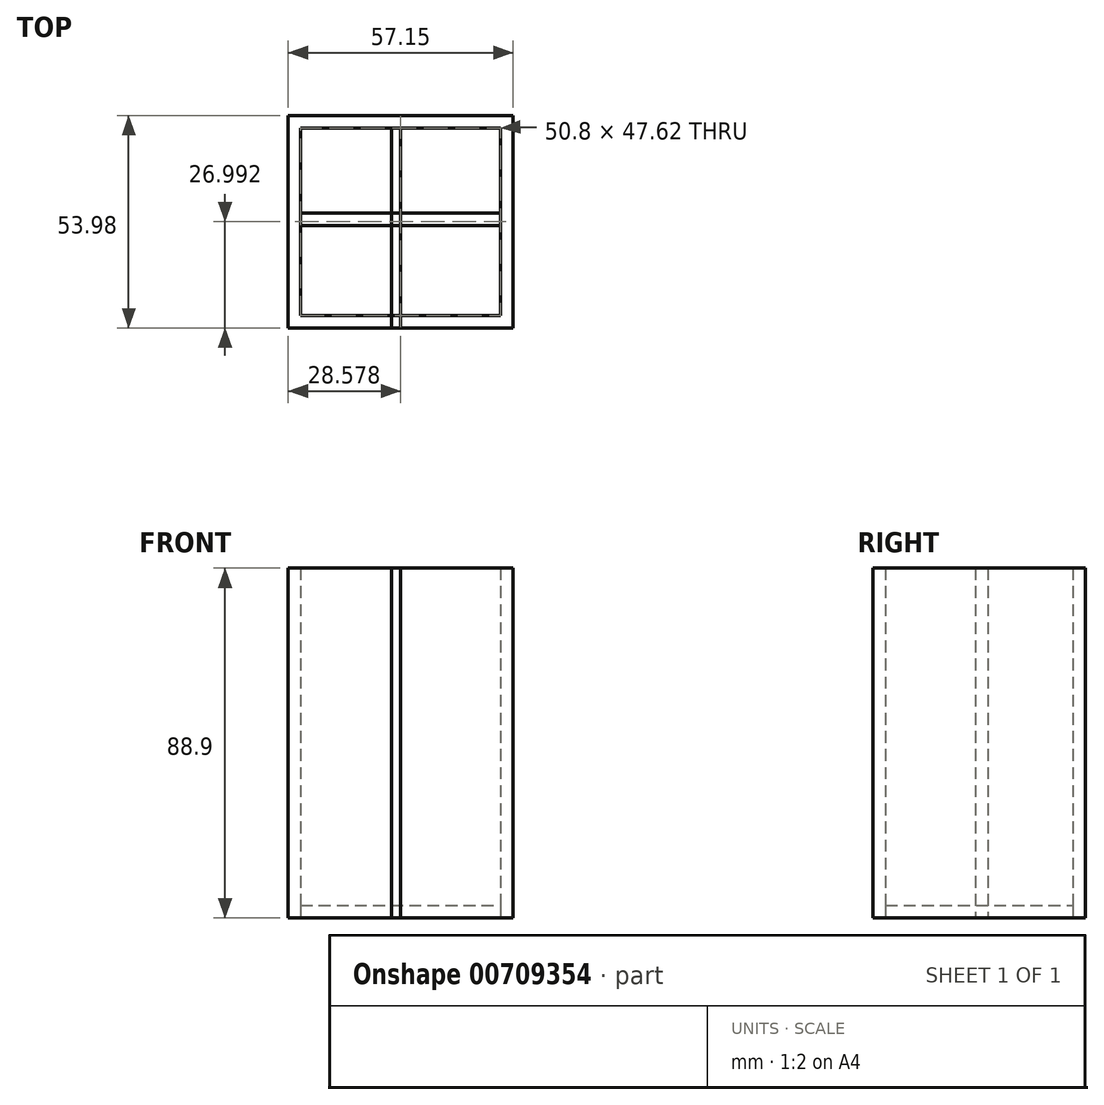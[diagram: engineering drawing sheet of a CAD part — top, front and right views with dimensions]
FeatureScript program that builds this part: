
annotation { "Feature Type Name" : "Feature", "Feature Type Description" : "" }
export const myFeature = defineFeature(function(context is Context, id is Id, definition is map)
    precondition{}
    {
        {
            var Q0;
            Q0=qCreatedBy(makeId("Front.planeOp"),FACE);
            var sketch = newSketch(context, id + "F0", { "sketchPlane" : qUnion([Q0])});
            skLineSegment(sketch, "E0.bottom", {"start": v(-26.25, 48.47) * mm, "end": v(30.9, 48.47) * mm});
            skLineSegment(sketch, "E0.top", {"start": v(-26.25, -40.43) * mm, "end": v(30.9, -40.43) * mm});
            skLineSegment(sketch, "E0.left", {"start": v(-26.25, 48.47) * mm, "end": v(-26.25, -40.43) * mm});
            skLineSegment(sketch, "E0.right", {"start": v(30.9, 48.47) * mm, "end": v(30.9, -40.43) * mm});
            skSolve(sketch);
        }
        {
            var Q0;
            Q0=makeQuery(id+"F0.imprint","IMPRINT",FACE,{"disambiguationData":[TD([[makeQuery(id+"F0.imprint","IMPRINT",EDGE,{"derivedFrom":sQuery(id+"F0.wireOp",EDGE,"E0.bottom")}),-1.0]])]});
            extrude(context, id + "F1", {"entities" : qUnion([Q0]), "depth" : 3.17 * mm, "offsetDistance" : 25.4 * mm});
        }
        {
            var Q0;
            Q0=makeQuery(id+"F1.opExtrude","CAP_FACE",FACE,{"disambiguationData":[OSD([sQuery(id+"F0.wireOp",EDGE,"E0.bottom"),sQuery(id+"F0.wireOp",EDGE,"E0.top"),sQuery(id+"F0.wireOp",EDGE,"E0.left"),sQuery(id+"F0.wireOp",EDGE,"E0.right")])],"isStart":false});
            var sketch = newSketch(context, id + "F2", { "sketchPlane" : qUnion([Q0])});
            skLineSegment(sketch, "E1.bottom", {"start": v(-26.25, 48.47) * mm, "end": v(-23.07, 48.47) * mm});
            skLineSegment(sketch, "E1.top", {"start": v(-26.25, -40.43) * mm, "end": v(-23.07, -40.43) * mm});
            skLineSegment(sketch, "E1.left", {"start": v(-26.25, 48.47) * mm, "end": v(-26.25, -40.43) * mm});
            skLineSegment(sketch, "E1.right", {"start": v(-23.07, 48.47) * mm, "end": v(-23.07, -40.43) * mm});
            skSolve(sketch);
        }
        {
            var Q0;
            Q0=makeQuery(id+"F2.imprint","IMPRINT",FACE,{"disambiguationData":[TD([[makeQuery(id+"F2.imprint","IMPRINT",EDGE,{"derivedFrom":sQuery(id+"F2.wireOp",EDGE,"E1.bottom")}),-1.0]])]});
            extrude(context, id + "F3", {"entities" : qUnion([Q0]), "operationType" : NewBodyOperationType.ADD, "depth" : 50.8 * mm, "offsetDistance" : 25.4 * mm});
        }
        {
            var Q0;
            Q0=makeQuery(id+"F1.opExtrude","CAP_FACE",FACE,{"disambiguationData":[OSD([sQuery(id+"F0.wireOp",EDGE,"E0.bottom"),sQuery(id+"F0.wireOp",EDGE,"E0.top"),sQuery(id+"F0.wireOp",EDGE,"E0.left"),sQuery(id+"F0.wireOp",EDGE,"E0.right")])],"isStart":false});
            var sketch = newSketch(context, id + "F4", { "sketchPlane" : qUnion([Q0])});
            skLineSegment(sketch, "E2.bottom", {"start": v(30.9, 48.47) * mm, "end": v(27.73, 48.47) * mm});
            skLineSegment(sketch, "E2.top", {"start": v(30.9, -40.43) * mm, "end": v(27.73, -40.43) * mm});
            skLineSegment(sketch, "E2.left", {"start": v(30.9, 48.47) * mm, "end": v(30.9, -40.43) * mm});
            skLineSegment(sketch, "E2.right", {"start": v(27.73, 48.47) * mm, "end": v(27.73, -40.43) * mm});
            skSolve(sketch);
        }
        {
            var Q0;
            Q0=makeQuery(id+"F4.imprint","IMPRINT",FACE,{"disambiguationData":[TD([[makeQuery(id+"F4.imprint","IMPRINT",EDGE,{"derivedFrom":sQuery(id+"F4.wireOp",EDGE,"E2.bottom")}),-1.0]])]});
            extrude(context, id + "F5", {"entities" : qUnion([Q0]), "operationType" : NewBodyOperationType.ADD, "depth" : 50.8 * mm, "offsetDistance" : 25.4 * mm});
        }
        {
            var Q0;
            Q0=makeQuery(id+"F3.opExtrude","CAP_FACE",FACE,{"disambiguationData":[OSD([sQuery(id+"F2.wireOp",EDGE,"E1.bottom"),sQuery(id+"F2.wireOp",EDGE,"E1.top"),sQuery(id+"F2.wireOp",EDGE,"E1.left"),sQuery(id+"F2.wireOp",EDGE,"E1.right")])],"isStart":false});
            var sketch = newSketch(context, id + "F6", { "sketchPlane" : qUnion([Q0])});
            skLineSegment(sketch, "E3.bottom", {"start": v(-26.25, 48.47) * mm, "end": v(30.9, 48.47) * mm});
            skLineSegment(sketch, "E3.top", {"start": v(-26.25, -40.43) * mm, "end": v(30.9, -40.43) * mm});
            skLineSegment(sketch, "E3.left", {"start": v(-26.25, 48.47) * mm, "end": v(-26.25, -40.43) * mm});
            skLineSegment(sketch, "E3.right", {"start": v(30.9, 48.47) * mm, "end": v(30.9, -40.43) * mm});
            skSolve(sketch);
        }
        {
            var Q0;
            {var subQ2=sQuery(id+"F6.wireOp",EDGE,"E3.right");Q0=makeQuery(id+"F6.imprint","IMPRINT",FACE,{"disambiguationData":[TD([[makeQuery(id+"F6.imprint","IMPRINT",EDGE,{"derivedFrom":subQ2}),-1.0]])]});}
            extrude(context, id + "F7", {"entities" : qUnion([Q0]), "operationType" : NewBodyOperationType.ADD, "oppositeDirection" : true, "depth" : 3.17 * mm, "offsetDistance" : 25.4 * mm});
        }
        {
            var Q0;
            Q0=makeQuery(id+"F7.boolean.opBoolean","MERGE",FACE,{"derivedFrom":[makeQuery(id+"F5.boolean.opBoolean","MERGE",FACE,{"derivedFrom":[makeQuery(id+"F3.boolean.opBoolean","MERGE",FACE,{"derivedFrom":[makeQuery(id+"F1.opExtrude","SWEPT_FACE",FACE,{"disambiguationData":[OSD([sQuery(id+"F0.wireOp",EDGE,"E0.top")])]}),makeQuery(id+"F3.opExtrude","SWEPT_FACE",FACE,{"disambiguationData":[OSD([sQuery(id+"F2.wireOp",EDGE,"E1.top")])]})]}),makeQuery(id+"F5.opExtrude","SWEPT_FACE",FACE,{"disambiguationData":[OSD([sQuery(id+"F4.wireOp",EDGE,"E2.top")])]})]}),makeQuery(id+"F7.opExtrude","SWEPT_FACE",FACE,{"disambiguationData":[OSD([sQuery(id+"F6.wireOp",EDGE,"E3.top")])]})]});
            var sketch = newSketch(context, id + "F8", { "sketchPlane" : qUnion([Q0])});
            skLineSegment(sketch, "E4.bottom", {"start": v(-23.07, 50.8) * mm, "end": v(27.73, 50.8) * mm});
            skLineSegment(sketch, "E4.top", {"start": v(-23.07, 3.18) * mm, "end": v(27.73, 3.18) * mm});
            skLineSegment(sketch, "E4.left", {"start": v(-23.07, 50.8) * mm, "end": v(-23.07, 3.18) * mm});
            skLineSegment(sketch, "E4.right", {"start": v(27.73, 50.8) * mm, "end": v(27.73, 3.18) * mm});
            skSolve(sketch);
        }
        {
            var Q0;
            Q0=makeQuery(id+"F8.imprint","IMPRINT",FACE,{"disambiguationData":[TD([[makeQuery(id+"F8.imprint","IMPRINT",EDGE,{"derivedFrom":sQuery(id+"F8.wireOp",EDGE,"E4.bottom")}),-1.0]])]});
            extrude(context, id + "F9", {"entities" : qUnion([Q0]), "oppositeDirection" : true, "depth" : 3.17 * mm, "offsetDistance" : 25.4 * mm});
        }
        {
            var Q0;
            Q0=makeQuery(id+"F1.opExtrude","CAP_FACE",FACE,{"disambiguationData":[OSD([sQuery(id+"F0.wireOp",EDGE,"E0.bottom"),sQuery(id+"F0.wireOp",EDGE,"E0.top"),sQuery(id+"F0.wireOp",EDGE,"E0.left"),sQuery(id+"F0.wireOp",EDGE,"E0.right")])],"isStart":false});
            var sketch = newSketch(context, id + "F10", { "sketchPlane" : qUnion([Q0])});
            skLineSegment(sketch, "E5.bottom", {"start": v(0, 48.47) * mm, "end": v(2.33, 48.47) * mm});
            skLineSegment(sketch, "E5.top", {"start": v(0, -40.43) * mm, "end": v(2.33, -40.43) * mm});
            skLineSegment(sketch, "E5.left", {"start": v(0, 48.47) * mm, "end": v(0, -40.43) * mm});
            skLineSegment(sketch, "E5.right", {"start": v(2.33, 48.47) * mm, "end": v(2.33, -40.43) * mm});
            skSolve(sketch);
        }
        {
            var Q0;
            Q0=makeQuery(id+"F10.imprint","IMPRINT",FACE,{"disambiguationData":[TD([[makeQuery(id+"F10.imprint","IMPRINT",EDGE,{"derivedFrom":sQuery(id+"F10.wireOp",EDGE,"E5.bottom")}),-1.0]])]});
            extrude(context, id + "F11", {"entities" : qUnion([Q0]), "depth" : 50.8 * mm, "offsetDistance" : 25.4 * mm});
        }
        {
            var Q0;
            Q0=makeQuery(id+"F5.opExtrude","SWEPT_FACE",FACE,{"disambiguationData":[OSD([sQuery(id+"F4.wireOp",EDGE,"E2.right")])]});
            var sketch = newSketch(context, id + "F12", { "sketchPlane" : qUnion([Q0])});
            skLineSegment(sketch, "E6.bottom", {"start": v(24.81, 48.47) * mm, "end": v(27.99, 48.47) * mm});
            skLineSegment(sketch, "E6.top", {"start": v(24.81, -40.43) * mm, "end": v(27.99, -40.43) * mm});
            skLineSegment(sketch, "E6.left", {"start": v(24.81, 48.47) * mm, "end": v(24.81, -40.43) * mm});
            skLineSegment(sketch, "E6.right", {"start": v(27.99, 48.47) * mm, "end": v(27.99, -40.43) * mm});
            skSolve(sketch);
        }
        {
            var Q0;
            Q0=makeQuery(id+"F12.imprint","IMPRINT",FACE,{"disambiguationData":[TD([[makeQuery(id+"F12.imprint","IMPRINT",EDGE,{"derivedFrom":sQuery(id+"F12.wireOp",EDGE,"E6.bottom")}),1.0]])]});
            extrude(context, id + "F13", {"entities" : qUnion([Q0]), "depth" : 50.8 * mm, "offsetDistance" : 25.4 * mm});
        }
    });
